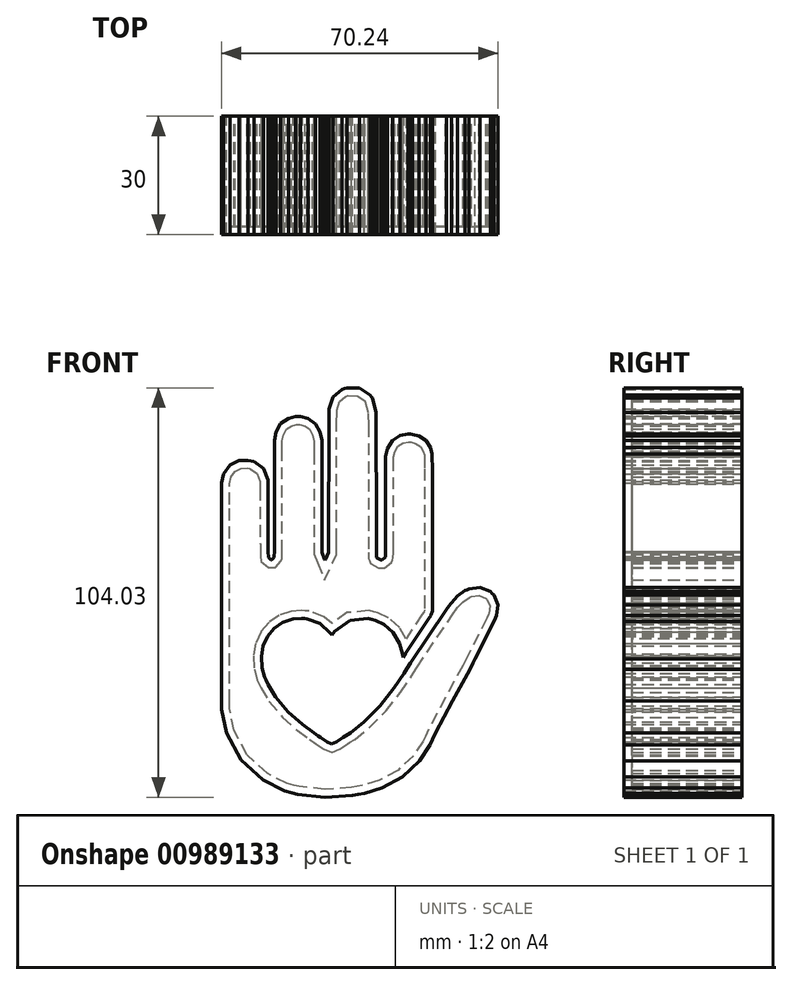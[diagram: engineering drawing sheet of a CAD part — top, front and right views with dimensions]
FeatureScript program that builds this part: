
annotation { "Feature Type Name" : "Feature", "Feature Type Description" : "" }
export const myFeature = defineFeature(function(context is Context, id is Id, definition is map)
    precondition{}
    {
        {
            var Q0;
            Q0=qCreatedBy(makeId("Front.planeOp"),FACE);
            var sketch = newSketch(context, id + "F0", { "sketchPlane" : qUnion([Q0])});
            skLineSegment(sketch, "E0", {"start": v(0.03, 0.14) * mm, "end": v(0.02, 0.14) * mm});
            skLineSegment(sketch, "E1", {"start": v(0.02, 0.14) * mm, "end": v(-0.03, 0.14) * mm});
            skLineSegment(sketch, "E2", {"start": v(-0.03, 0.14) * mm, "end": v(-0.07, 0.1) * mm});
            skLineSegment(sketch, "E3", {"start": v(-0.07, 0.1) * mm, "end": v(-0.07, 0.1) * mm});
            skLineSegment(sketch, "E4", {"start": v(-0.07, 0.1) * mm, "end": v(-0.08, 0.1) * mm});
            skLineSegment(sketch, "E5", {"start": v(-0.08, 0.1) * mm, "end": v(-0.1, 0.13) * mm});
            skLineSegment(sketch, "E6", {"start": v(-0.1, 0.13) * mm, "end": v(-0.14, 0.14) * mm});
            skLineSegment(sketch, "E7", {"start": v(-0.14, 0.14) * mm, "end": v(-0.14, 0.14) * mm});
            skLineSegment(sketch, "E8", {"start": v(-0.14, 0.14) * mm, "end": v(-0.15, 0.14) * mm});
            skLineSegment(sketch, "E9", {"start": v(-0.15, 0.14) * mm, "end": v(-0.17, 0.14) * mm});
            skLineSegment(sketch, "E10", {"start": v(-0.17, 0.14) * mm, "end": v(-0.2, 0.13) * mm});
            skLineSegment(sketch, "E11", {"start": v(-0.2, 0.13) * mm, "end": v(-0.22, 0.12) * mm});
            skLineSegment(sketch, "E12", {"start": v(-0.22, 0.12) * mm, "end": v(-0.24, 0.1) * mm});
            skLineSegment(sketch, "E13", {"start": v(-0.24, 0.1) * mm, "end": v(-0.25, 0.07) * mm});
            skLineSegment(sketch, "E14", {"start": v(-0.25, 0.07) * mm, "end": v(-0.25, 0.05) * mm});
            skLineSegment(sketch, "E15", {"start": v(-0.25, 0.05) * mm, "end": v(-0.25, 0.02) * mm});
            skLineSegment(sketch, "E16", {"start": v(-0.25, 0.02) * mm, "end": v(-0.24, 0) * mm});
            skLineSegment(sketch, "E17", {"start": v(-0.24, 0) * mm, "end": v(-0.24, -0.01) * mm});
            skLineSegment(sketch, "E18", {"start": v(-0.24, -0.01) * mm, "end": v(-0.24, -0.03) * mm});
            skLineSegment(sketch, "E19", {"start": v(-0.24, -0.03) * mm, "end": v(-0.22, -0.06) * mm});
            skLineSegment(sketch, "E20", {"start": v(-0.22, -0.06) * mm, "end": v(-0.18, -0.1) * mm});
            skLineSegment(sketch, "E21", {"start": v(-0.18, -0.1) * mm, "end": v(-0.15, -0.13) * mm});
            skLineSegment(sketch, "E22", {"start": v(-0.15, -0.13) * mm, "end": v(-0.12, -0.15) * mm});
            skLineSegment(sketch, "E23", {"start": v(-0.12, -0.15) * mm, "end": v(-0.1, -0.16) * mm});
            skLineSegment(sketch, "E24", {"start": v(-0.1, -0.16) * mm, "end": v(-0.1, -0.16) * mm});
            skLineSegment(sketch, "E25", {"start": v(-0.1, -0.16) * mm, "end": v(-0.09, -0.17) * mm});
            skLineSegment(sketch, "E26", {"start": v(-0.09, -0.17) * mm, "end": v(-0.07, -0.18) * mm});
            skLineSegment(sketch, "E27", {"start": v(-0.07, -0.18) * mm, "end": v(-0.06, -0.17) * mm});
            skLineSegment(sketch, "E28", {"start": v(-0.06, -0.17) * mm, "end": v(-0.04, -0.16) * mm});
            skLineSegment(sketch, "E29", {"start": v(-0.04, -0.16) * mm, "end": v(-0.04, -0.16) * mm});
            skLineSegment(sketch, "E30", {"start": v(-0.04, -0.16) * mm, "end": v(-0.03, -0.15) * mm});
            skLineSegment(sketch, "E31", {"start": v(-0.03, -0.15) * mm, "end": v(0, -0.12) * mm});
            skLineSegment(sketch, "E32", {"start": v(0, -0.12) * mm, "end": v(0.05, -0.08) * mm});
            skLineSegment(sketch, "E33", {"start": v(0.05, -0.08) * mm, "end": v(0.08, -0.03) * mm});
            skLineSegment(sketch, "E34", {"start": v(0.08, -0.03) * mm, "end": v(0.1, 0) * mm});
            skLineSegment(sketch, "E35", {"start": v(0.1, 0) * mm, "end": v(0.12, 0.01) * mm});
            skLineSegment(sketch, "E36", {"start": v(0.12, 0.01) * mm, "end": v(0.13, 0.03) * mm});
            skLineSegment(sketch, "E37", {"start": v(0.13, 0.03) * mm, "end": v(0.22, 0.17) * mm});
            skLineSegment(sketch, "E38", {"start": v(0.22, 0.17) * mm, "end": v(0.23, 0.18) * mm});
            skLineSegment(sketch, "E39", {"start": v(0.23, 0.18) * mm, "end": v(0.23, 0.18) * mm});
            skLineSegment(sketch, "E40", {"start": v(0.23, 0.18) * mm, "end": v(0.25, 0.2) * mm});
            skLineSegment(sketch, "E41", {"start": v(0.25, 0.2) * mm, "end": v(0.27, 0.21) * mm});
            skLineSegment(sketch, "E42", {"start": v(0.27, 0.21) * mm, "end": v(0.27, 0.21) * mm});
            skLineSegment(sketch, "E43", {"start": v(0.27, 0.21) * mm, "end": v(0.28, 0.22) * mm});
            skLineSegment(sketch, "E44", {"start": v(0.28, 0.22) * mm, "end": v(0.3, 0.22) * mm});
            skLineSegment(sketch, "E45", {"start": v(0.3, 0.22) * mm, "end": v(0.33, 0.21) * mm});
            skLineSegment(sketch, "E46", {"start": v(0.33, 0.21) * mm, "end": v(0.33, 0.2) * mm});
            skLineSegment(sketch, "E47", {"start": v(0.33, 0.2) * mm, "end": v(0.34, 0.2) * mm});
            skLineSegment(sketch, "E48", {"start": v(0.34, 0.2) * mm, "end": v(0.35, 0.18) * mm});
            skLineSegment(sketch, "E49", {"start": v(0.35, 0.18) * mm, "end": v(0.35, 0.15) * mm});
            skLineSegment(sketch, "E50", {"start": v(0.35, 0.15) * mm, "end": v(0.34, 0.14) * mm});
            skLineSegment(sketch, "E51", {"start": v(0.34, 0.14) * mm, "end": v(0.34, 0.13) * mm});
            skLineSegment(sketch, "E52", {"start": v(0.34, 0.13) * mm, "end": v(0.3, 0.04) * mm});
            skLineSegment(sketch, "E53", {"start": v(0.3, 0.04) * mm, "end": v(0.29, 0.03) * mm});
            skLineSegment(sketch, "E54", {"start": v(0.29, 0.03) * mm, "end": v(0.28, 0.01) * mm});
            skLineSegment(sketch, "E55", {"start": v(0.28, 0.01) * mm, "end": v(0.23, -0.07) * mm});
            skLineSegment(sketch, "E56", {"start": v(0.23, -0.07) * mm, "end": v(0.2, -0.15) * mm});
            skLineSegment(sketch, "E57", {"start": v(0.2, -0.15) * mm, "end": v(0.18, -0.17) * mm});
            skLineSegment(sketch, "E58", {"start": v(0.18, -0.17) * mm, "end": v(0.18, -0.18) * mm});
            skLineSegment(sketch, "E59", {"start": v(0.18, -0.18) * mm, "end": v(0.15, -0.22) * mm});
            skLineSegment(sketch, "E60", {"start": v(0.15, -0.22) * mm, "end": v(0.1, -0.26) * mm});
            skLineSegment(sketch, "E61", {"start": v(0.1, -0.26) * mm, "end": v(0.05, -0.29) * mm});
            skLineSegment(sketch, "E62", {"start": v(0.05, -0.29) * mm, "end": v(0, -0.3) * mm});
            skLineSegment(sketch, "E63", {"start": v(0, -0.3) * mm, "end": v(0, -0.3) * mm});
            skLineSegment(sketch, "E64", {"start": v(0, -0.3) * mm, "end": v(-0.02, -0.3) * mm});
            skLineSegment(sketch, "E65", {"start": v(-0.02, -0.3) * mm, "end": v(-0.1, -0.31) * mm});
            skLineSegment(sketch, "E66", {"start": v(-0.1, -0.31) * mm, "end": v(-0.16, -0.3) * mm});
            skLineSegment(sketch, "E67", {"start": v(-0.16, -0.3) * mm, "end": v(-0.17, -0.3) * mm});
            skLineSegment(sketch, "E68", {"start": v(-0.17, -0.3) * mm, "end": v(-0.2, -0.3) * mm});
            skLineSegment(sketch, "E69", {"start": v(-0.2, -0.3) * mm, "end": v(-0.25, -0.27) * mm});
            skLineSegment(sketch, "E70", {"start": v(-0.25, -0.27) * mm, "end": v(-0.3, -0.22) * mm});
            skLineSegment(sketch, "E71", {"start": v(-0.3, -0.22) * mm, "end": v(-0.34, -0.15) * mm});
            skLineSegment(sketch, "E72", {"start": v(-0.34, -0.15) * mm, "end": v(-0.35, -0.09) * mm});
            skLineSegment(sketch, "E73", {"start": v(-0.35, -0.09) * mm, "end": v(-0.35, -0.07) * mm});
            skLineSegment(sketch, "E74", {"start": v(-0.35, -0.07) * mm, "end": v(-0.35, -0.02) * mm});
            skLineSegment(sketch, "E75", {"start": v(-0.35, -0.02) * mm, "end": v(-0.35, 0.43) * mm});
            skLineSegment(sketch, "E76", {"start": v(-0.35, 0.43) * mm, "end": v(-0.35, 0.48) * mm});
            skLineSegment(sketch, "E77", {"start": v(-0.35, 0.48) * mm, "end": v(-0.35, 0.49) * mm});
            skLineSegment(sketch, "E78", {"start": v(-0.35, 0.49) * mm, "end": v(-0.35, 0.5) * mm});
            skLineSegment(sketch, "E79", {"start": v(-0.35, 0.5) * mm, "end": v(-0.33, 0.53) * mm});
            skLineSegment(sketch, "E80", {"start": v(-0.33, 0.53) * mm, "end": v(-0.3, 0.54) * mm});
            skLineSegment(sketch, "E81", {"start": v(-0.3, 0.54) * mm, "end": v(-0.29, 0.54) * mm});
            skLineSegment(sketch, "E82", {"start": v(-0.29, 0.54) * mm, "end": v(-0.28, 0.54) * mm});
            skLineSegment(sketch, "E83", {"start": v(-0.28, 0.54) * mm, "end": v(-0.27, 0.54) * mm});
            skLineSegment(sketch, "E84", {"start": v(-0.27, 0.54) * mm, "end": v(-0.25, 0.52) * mm});
            skLineSegment(sketch, "E85", {"start": v(-0.25, 0.52) * mm, "end": v(-0.24, 0.5) * mm});
            skLineSegment(sketch, "E86", {"start": v(-0.24, 0.5) * mm, "end": v(-0.24, 0.49) * mm});
            skLineSegment(sketch, "E87", {"start": v(-0.24, 0.49) * mm, "end": v(-0.24, 0.47) * mm});
            skLineSegment(sketch, "E88", {"start": v(-0.24, 0.47) * mm, "end": v(-0.24, 0.33) * mm});
            skLineSegment(sketch, "E89", {"start": v(-0.24, 0.33) * mm, "end": v(-0.23, 0.32) * mm});
            skLineSegment(sketch, "E90", {"start": v(-0.23, 0.32) * mm, "end": v(-0.23, 0.31) * mm});
            skLineSegment(sketch, "E91", {"start": v(-0.23, 0.31) * mm, "end": v(-0.23, 0.3) * mm});
            skLineSegment(sketch, "E92", {"start": v(-0.23, 0.3) * mm, "end": v(-0.23, 0.3) * mm});
            skLineSegment(sketch, "E93", {"start": v(-0.23, 0.3) * mm, "end": v(-0.22, 0.3) * mm});
            skLineSegment(sketch, "E94", {"start": v(-0.22, 0.3) * mm, "end": v(-0.22, 0.3) * mm});
            skLineSegment(sketch, "E95", {"start": v(-0.22, 0.3) * mm, "end": v(-0.22, 0.31) * mm});
            skLineSegment(sketch, "E96", {"start": v(-0.22, 0.31) * mm, "end": v(-0.22, 0.32) * mm});
            skLineSegment(sketch, "E97", {"start": v(-0.22, 0.32) * mm, "end": v(-0.22, 0.38) * mm});
            skLineSegment(sketch, "E98", {"start": v(-0.22, 0.38) * mm, "end": v(-0.22, 0.56) * mm});
            skLineSegment(sketch, "E99", {"start": v(-0.22, 0.56) * mm, "end": v(-0.22, 0.59) * mm});
            skLineSegment(sketch, "E100", {"start": v(-0.22, 0.59) * mm, "end": v(-0.22, 0.6) * mm});
            skLineSegment(sketch, "E101", {"start": v(-0.22, 0.6) * mm, "end": v(-0.22, 0.62) * mm});
            skLineSegment(sketch, "E102", {"start": v(-0.22, 0.62) * mm, "end": v(-0.2, 0.64) * mm});
            skLineSegment(sketch, "E103", {"start": v(-0.2, 0.64) * mm, "end": v(-0.18, 0.65) * mm});
            skLineSegment(sketch, "E104", {"start": v(-0.18, 0.65) * mm, "end": v(-0.16, 0.65) * mm});
            skLineSegment(sketch, "E105", {"start": v(-0.16, 0.65) * mm, "end": v(-0.16, 0.65) * mm});
            skLineSegment(sketch, "E106", {"start": v(-0.16, 0.65) * mm, "end": v(-0.15, 0.65) * mm});
            skLineSegment(sketch, "E107", {"start": v(-0.15, 0.65) * mm, "end": v(-0.13, 0.65) * mm});
            skLineSegment(sketch, "E108", {"start": v(-0.13, 0.65) * mm, "end": v(-0.11, 0.64) * mm});
            skLineSegment(sketch, "E109", {"start": v(-0.11, 0.64) * mm, "end": v(-0.1, 0.62) * mm});
            skLineSegment(sketch, "E110", {"start": v(-0.1, 0.62) * mm, "end": v(-0.1, 0.6) * mm});
            skLineSegment(sketch, "E111", {"start": v(-0.1, 0.6) * mm, "end": v(-0.1, 0.59) * mm});
            skLineSegment(sketch, "E112", {"start": v(-0.1, 0.59) * mm, "end": v(-0.1, 0.56) * mm});
            skLineSegment(sketch, "E113", {"start": v(-0.1, 0.56) * mm, "end": v(-0.1, 0.33) * mm});
            skLineSegment(sketch, "E114", {"start": v(-0.1, 0.33) * mm, "end": v(-0.1, 0.31) * mm});
            skLineSegment(sketch, "E115", {"start": v(-0.1, 0.31) * mm, "end": v(-0.1, 0.3) * mm});
            skLineSegment(sketch, "E116", {"start": v(-0.1, 0.3) * mm, "end": v(-0.1, 0.3) * mm});
            skLineSegment(sketch, "E117", {"start": v(-0.1, 0.3) * mm, "end": v(-0.09, 0.3) * mm});
            skLineSegment(sketch, "E118", {"start": v(-0.09, 0.3) * mm, "end": v(-0.08, 0.3) * mm});
            skLineSegment(sketch, "E119", {"start": v(-0.08, 0.3) * mm, "end": v(-0.08, 0.31) * mm});
            skLineSegment(sketch, "E120", {"start": v(-0.08, 0.31) * mm, "end": v(-0.08, 0.34) * mm});
            skLineSegment(sketch, "E121", {"start": v(-0.08, 0.34) * mm, "end": v(-0.08, 0.64) * mm});
            skLineSegment(sketch, "E122", {"start": v(-0.08, 0.64) * mm, "end": v(-0.08, 0.67) * mm});
            skLineSegment(sketch, "E123", {"start": v(-0.08, 0.67) * mm, "end": v(-0.08, 0.67) * mm});
            skLineSegment(sketch, "E124", {"start": v(-0.08, 0.67) * mm, "end": v(-0.07, 0.7) * mm});
            skLineSegment(sketch, "E125", {"start": v(-0.07, 0.7) * mm, "end": v(-0.05, 0.72) * mm});
            skLineSegment(sketch, "E126", {"start": v(-0.05, 0.72) * mm, "end": v(-0.04, 0.73) * mm});
            skLineSegment(sketch, "E127", {"start": v(-0.04, 0.73) * mm, "end": v(-0.04, 0.73) * mm});
            skLineSegment(sketch, "E128", {"start": v(-0.04, 0.73) * mm, "end": v(0, 0.73) * mm});
            skLineSegment(sketch, "E129", {"start": v(0, 0.73) * mm, "end": v(0.02, 0.71) * mm});
            skLineSegment(sketch, "E130", {"start": v(0.02, 0.71) * mm, "end": v(0.03, 0.7) * mm});
            skLineSegment(sketch, "E131", {"start": v(0.03, 0.7) * mm, "end": v(0.03, 0.7) * mm});
            skLineSegment(sketch, "E132", {"start": v(0.03, 0.7) * mm, "end": v(0.04, 0.67) * mm});
            skLineSegment(sketch, "E133", {"start": v(0.04, 0.67) * mm, "end": v(0.04, 0.66) * mm});
            skLineSegment(sketch, "E134", {"start": v(0.04, 0.66) * mm, "end": v(0.04, 0.63) * mm});
            skLineSegment(sketch, "E135", {"start": v(0.04, 0.63) * mm, "end": v(0.04, 0.4) * mm});
            skLineSegment(sketch, "E136", {"start": v(0.04, 0.4) * mm, "end": v(0.04, 0.32) * mm});
            skLineSegment(sketch, "E137", {"start": v(0.04, 0.32) * mm, "end": v(0.04, 0.31) * mm});
            skLineSegment(sketch, "E138", {"start": v(0.04, 0.31) * mm, "end": v(0.04, 0.3) * mm});
            skLineSegment(sketch, "E139", {"start": v(0.04, 0.3) * mm, "end": v(0.04, 0.3) * mm});
            skLineSegment(sketch, "E140", {"start": v(0.04, 0.3) * mm, "end": v(0.05, 0.3) * mm});
            skLineSegment(sketch, "E141", {"start": v(0.05, 0.3) * mm, "end": v(0.05, 0.3) * mm});
            skLineSegment(sketch, "E142", {"start": v(0.05, 0.3) * mm, "end": v(0.06, 0.3) * mm});
            skLineSegment(sketch, "E143", {"start": v(0.06, 0.3) * mm, "end": v(0.06, 0.3) * mm});
            skLineSegment(sketch, "E144", {"start": v(0.06, 0.3) * mm, "end": v(0.06, 0.31) * mm});
            skLineSegment(sketch, "E145", {"start": v(0.06, 0.31) * mm, "end": v(0.06, 0.33) * mm});
            skLineSegment(sketch, "E146", {"start": v(0.06, 0.33) * mm, "end": v(0.06, 0.53) * mm});
            skLineSegment(sketch, "E147", {"start": v(0.06, 0.53) * mm, "end": v(0.06, 0.55) * mm});
            skLineSegment(sketch, "E148", {"start": v(0.06, 0.55) * mm, "end": v(0.06, 0.55) * mm});
            skLineSegment(sketch, "E149", {"start": v(0.06, 0.55) * mm, "end": v(0.07, 0.57) * mm});
            skLineSegment(sketch, "E150", {"start": v(0.07, 0.57) * mm, "end": v(0.08, 0.6) * mm});
            skLineSegment(sketch, "E151", {"start": v(0.08, 0.6) * mm, "end": v(0.1, 0.6) * mm});
            skLineSegment(sketch, "E152", {"start": v(0.1, 0.6) * mm, "end": v(0.12, 0.61) * mm});
            skLineSegment(sketch, "E153", {"start": v(0.12, 0.61) * mm, "end": v(0.13, 0.61) * mm});
            skLineSegment(sketch, "E154", {"start": v(0.13, 0.61) * mm, "end": v(0.13, 0.6) * mm});
            skLineSegment(sketch, "E155", {"start": v(0.13, 0.6) * mm, "end": v(0.15, 0.6) * mm});
            skLineSegment(sketch, "E156", {"start": v(0.15, 0.6) * mm, "end": v(0.17, 0.6) * mm});
            skLineSegment(sketch, "E157", {"start": v(0.17, 0.6) * mm, "end": v(0.18, 0.58) * mm});
            skLineSegment(sketch, "E158", {"start": v(0.18, 0.58) * mm, "end": v(0.18, 0.56) * mm});
            skLineSegment(sketch, "E159", {"start": v(0.18, 0.56) * mm, "end": v(0.18, 0.55) * mm});
            skLineSegment(sketch, "E160", {"start": v(0.18, 0.55) * mm, "end": v(0.18, 0.52) * mm});
            skLineSegment(sketch, "E161", {"start": v(0.18, 0.52) * mm, "end": v(0.18, 0.2) * mm});
            skLineSegment(sketch, "E162", {"start": v(0.18, 0.2) * mm, "end": v(0.18, 0.16) * mm});
            skLineSegment(sketch, "E163", {"start": v(0.18, 0.16) * mm, "end": v(0.18, 0.16) * mm});
            skLineSegment(sketch, "E164", {"start": v(0.18, 0.16) * mm, "end": v(0.18, 0.15) * mm});
            skLineSegment(sketch, "E165", {"start": v(0.18, 0.15) * mm, "end": v(0.18, 0.15) * mm});
            skLineSegment(sketch, "E166", {"start": v(0.18, 0.15) * mm, "end": v(0.17, 0.14) * mm});
            skLineSegment(sketch, "E167", {"start": v(0.17, 0.14) * mm, "end": v(0.11, 0.05) * mm});
            skLineSegment(sketch, "E168", {"start": v(0.11, 0.05) * mm, "end": v(0.1, 0.04) * mm});
            skLineSegment(sketch, "E169", {"start": v(0.1, 0.04) * mm, "end": v(0.1, 0.05) * mm});
            skLineSegment(sketch, "E170", {"start": v(0.1, 0.05) * mm, "end": v(0.1, 0.08) * mm});
            skLineSegment(sketch, "E171", {"start": v(0.1, 0.08) * mm, "end": v(0.08, 0.1) * mm});
            skLineSegment(sketch, "E172", {"start": v(0.08, 0.1) * mm, "end": v(0.06, 0.13) * mm});
            skLineSegment(sketch, "E173", {"start": v(0.06, 0.13) * mm, "end": v(0.04, 0.14) * mm});
            skLineSegment(sketch, "E174", {"start": v(0.04, 0.14) * mm, "end": v(0.03, 0.14) * mm});
            skSolve(sketch);
        }
        {
            var Q0;
            Q0=makeQuery(id+"F0.imprint","IMPRINT",FACE,{"disambiguationData":[TD([[makeQuery(id+"F0.imprint","IMPRINT",EDGE,{"derivedFrom":sQuery(id+"F0.wireOp",EDGE,"E0")}),-1.0]])]});
            extrude(context, id + "F1", {"entities" : qUnion([Q0]), "depth" : 0.2 * mm, "offsetDistance" : 25 * mm});
        }
        {
            var Q0;
            Q0=makeQuery(id+"F1.opExtrude","SWEPT_BODY",BODY,{"disambiguationData":[OSD([sQuery(id+"F0.wireOp",EDGE,"E0"),sQuery(id+"F0.wireOp",EDGE,"E1"),sQuery(id+"F0.wireOp",EDGE,"E2"),sQuery(id+"F0.wireOp",EDGE,"E3"),sQuery(id+"F0.wireOp",EDGE,"E4"),sQuery(id+"F0.wireOp",EDGE,"E5"),sQuery(id+"F0.wireOp",EDGE,"E6"),sQuery(id+"F0.wireOp",EDGE,"E7"),sQuery(id+"F0.wireOp",EDGE,"E8"),sQuery(id+"F0.wireOp",EDGE,"E9"),sQuery(id+"F0.wireOp",EDGE,"E10"),sQuery(id+"F0.wireOp",EDGE,"E11"),sQuery(id+"F0.wireOp",EDGE,"E12"),sQuery(id+"F0.wireOp",EDGE,"E13"),sQuery(id+"F0.wireOp",EDGE,"E14"),sQuery(id+"F0.wireOp",EDGE,"E15"),sQuery(id+"F0.wireOp",EDGE,"E16"),sQuery(id+"F0.wireOp",EDGE,"E17"),sQuery(id+"F0.wireOp",EDGE,"E18"),sQuery(id+"F0.wireOp",EDGE,"E19"),sQuery(id+"F0.wireOp",EDGE,"E20"),sQuery(id+"F0.wireOp",EDGE,"E21"),sQuery(id+"F0.wireOp",EDGE,"E22"),sQuery(id+"F0.wireOp",EDGE,"E23"),sQuery(id+"F0.wireOp",EDGE,"E24"),sQuery(id+"F0.wireOp",EDGE,"E25"),sQuery(id+"F0.wireOp",EDGE,"E26"),sQuery(id+"F0.wireOp",EDGE,"E27"),sQuery(id+"F0.wireOp",EDGE,"E28"),sQuery(id+"F0.wireOp",EDGE,"E29"),sQuery(id+"F0.wireOp",EDGE,"E30"),sQuery(id+"F0.wireOp",EDGE,"E31"),sQuery(id+"F0.wireOp",EDGE,"E32"),sQuery(id+"F0.wireOp",EDGE,"E33"),sQuery(id+"F0.wireOp",EDGE,"E34"),sQuery(id+"F0.wireOp",EDGE,"E35"),sQuery(id+"F0.wireOp",EDGE,"E36"),sQuery(id+"F0.wireOp",EDGE,"E37"),sQuery(id+"F0.wireOp",EDGE,"E38"),sQuery(id+"F0.wireOp",EDGE,"E39"),sQuery(id+"F0.wireOp",EDGE,"E40"),sQuery(id+"F0.wireOp",EDGE,"E41"),sQuery(id+"F0.wireOp",EDGE,"E42"),sQuery(id+"F0.wireOp",EDGE,"E43"),sQuery(id+"F0.wireOp",EDGE,"E44"),sQuery(id+"F0.wireOp",EDGE,"E45"),sQuery(id+"F0.wireOp",EDGE,"E46"),sQuery(id+"F0.wireOp",EDGE,"E47"),sQuery(id+"F0.wireOp",EDGE,"E48"),sQuery(id+"F0.wireOp",EDGE,"E49"),sQuery(id+"F0.wireOp",EDGE,"E50"),sQuery(id+"F0.wireOp",EDGE,"E51"),sQuery(id+"F0.wireOp",EDGE,"E52"),sQuery(id+"F0.wireOp",EDGE,"E53"),sQuery(id+"F0.wireOp",EDGE,"E54"),sQuery(id+"F0.wireOp",EDGE,"E55"),sQuery(id+"F0.wireOp",EDGE,"E56"),sQuery(id+"F0.wireOp",EDGE,"E57"),sQuery(id+"F0.wireOp",EDGE,"E58"),sQuery(id+"F0.wireOp",EDGE,"E59"),sQuery(id+"F0.wireOp",EDGE,"E60"),sQuery(id+"F0.wireOp",EDGE,"E61"),sQuery(id+"F0.wireOp",EDGE,"E62"),sQuery(id+"F0.wireOp",EDGE,"E63"),sQuery(id+"F0.wireOp",EDGE,"E64"),sQuery(id+"F0.wireOp",EDGE,"E65"),sQuery(id+"F0.wireOp",EDGE,"E66"),sQuery(id+"F0.wireOp",EDGE,"E67"),sQuery(id+"F0.wireOp",EDGE,"E68"),sQuery(id+"F0.wireOp",EDGE,"E69"),sQuery(id+"F0.wireOp",EDGE,"E70"),sQuery(id+"F0.wireOp",EDGE,"E71"),sQuery(id+"F0.wireOp",EDGE,"E72"),sQuery(id+"F0.wireOp",EDGE,"E73"),sQuery(id+"F0.wireOp",EDGE,"E74"),sQuery(id+"F0.wireOp",EDGE,"E75"),sQuery(id+"F0.wireOp",EDGE,"E76"),sQuery(id+"F0.wireOp",EDGE,"E77"),sQuery(id+"F0.wireOp",EDGE,"E78"),sQuery(id+"F0.wireOp",EDGE,"E79"),sQuery(id+"F0.wireOp",EDGE,"E80"),sQuery(id+"F0.wireOp",EDGE,"E81"),sQuery(id+"F0.wireOp",EDGE,"E82"),sQuery(id+"F0.wireOp",EDGE,"E83"),sQuery(id+"F0.wireOp",EDGE,"E84"),sQuery(id+"F0.wireOp",EDGE,"E85"),sQuery(id+"F0.wireOp",EDGE,"E86"),sQuery(id+"F0.wireOp",EDGE,"E87"),sQuery(id+"F0.wireOp",EDGE,"E88"),sQuery(id+"F0.wireOp",EDGE,"E89"),sQuery(id+"F0.wireOp",EDGE,"E90"),sQuery(id+"F0.wireOp",EDGE,"E91"),sQuery(id+"F0.wireOp",EDGE,"E92"),sQuery(id+"F0.wireOp",EDGE,"E92"),sQuery(id+"F0.wireOp",EDGE,"E92"),sQuery(id+"F0.wireOp",EDGE,"E92"),sQuery(id+"F0.wireOp",EDGE,"E92"),sQuery(id+"F0.wireOp",EDGE,"E93"),sQuery(id+"F0.wireOp",EDGE,"E94"),sQuery(id+"F0.wireOp",EDGE,"E94"),sQuery(id+"F0.wireOp",EDGE,"E95"),sQuery(id+"F0.wireOp",EDGE,"E96"),sQuery(id+"F0.wireOp",EDGE,"E97"),sQuery(id+"F0.wireOp",EDGE,"E98"),sQuery(id+"F0.wireOp",EDGE,"E99"),sQuery(id+"F0.wireOp",EDGE,"E100"),sQuery(id+"F0.wireOp",EDGE,"E101"),sQuery(id+"F0.wireOp",EDGE,"E102"),sQuery(id+"F0.wireOp",EDGE,"E103"),sQuery(id+"F0.wireOp",EDGE,"E104"),sQuery(id+"F0.wireOp",EDGE,"E105"),sQuery(id+"F0.wireOp",EDGE,"E106"),sQuery(id+"F0.wireOp",EDGE,"E107"),sQuery(id+"F0.wireOp",EDGE,"E108"),sQuery(id+"F0.wireOp",EDGE,"E109"),sQuery(id+"F0.wireOp",EDGE,"E110"),sQuery(id+"F0.wireOp",EDGE,"E111"),sQuery(id+"F0.wireOp",EDGE,"E112"),sQuery(id+"F0.wireOp",EDGE,"E113"),sQuery(id+"F0.wireOp",EDGE,"E114"),sQuery(id+"F0.wireOp",EDGE,"E115"),sQuery(id+"F0.wireOp",EDGE,"E116"),sQuery(id+"F0.wireOp",EDGE,"E116"),sQuery(id+"F0.wireOp",EDGE,"E117"),sQuery(id+"F0.wireOp",EDGE,"E118"),sQuery(id+"F0.wireOp",EDGE,"E119"),sQuery(id+"F0.wireOp",EDGE,"E120"),sQuery(id+"F0.wireOp",EDGE,"E121"),sQuery(id+"F0.wireOp",EDGE,"E122"),sQuery(id+"F0.wireOp",EDGE,"E123"),sQuery(id+"F0.wireOp",EDGE,"E124"),sQuery(id+"F0.wireOp",EDGE,"E125"),sQuery(id+"F0.wireOp",EDGE,"E126"),sQuery(id+"F0.wireOp",EDGE,"E127"),sQuery(id+"F0.wireOp",EDGE,"E128"),sQuery(id+"F0.wireOp",EDGE,"E129"),sQuery(id+"F0.wireOp",EDGE,"E130"),sQuery(id+"F0.wireOp",EDGE,"E131"),sQuery(id+"F0.wireOp",EDGE,"E132"),sQuery(id+"F0.wireOp",EDGE,"E133"),sQuery(id+"F0.wireOp",EDGE,"E134"),sQuery(id+"F0.wireOp",EDGE,"E135"),sQuery(id+"F0.wireOp",EDGE,"E136"),sQuery(id+"F0.wireOp",EDGE,"E137"),sQuery(id+"F0.wireOp",EDGE,"E138"),sQuery(id+"F0.wireOp",EDGE,"E139"),sQuery(id+"F0.wireOp",EDGE,"E139"),sQuery(id+"F0.wireOp",EDGE,"E140"),sQuery(id+"F0.wireOp",EDGE,"E141"),sQuery(id+"F0.wireOp",EDGE,"E141"),sQuery(id+"F0.wireOp",EDGE,"E142"),sQuery(id+"F0.wireOp",EDGE,"E143"),sQuery(id+"F0.wireOp",EDGE,"E143"),sQuery(id+"F0.wireOp",EDGE,"E143"),sQuery(id+"F0.wireOp",EDGE,"E144"),sQuery(id+"F0.wireOp",EDGE,"E145"),sQuery(id+"F0.wireOp",EDGE,"E146"),sQuery(id+"F0.wireOp",EDGE,"E147"),sQuery(id+"F0.wireOp",EDGE,"E148"),sQuery(id+"F0.wireOp",EDGE,"E149"),sQuery(id+"F0.wireOp",EDGE,"E150"),sQuery(id+"F0.wireOp",EDGE,"E151"),sQuery(id+"F0.wireOp",EDGE,"E152"),sQuery(id+"F0.wireOp",EDGE,"E153"),sQuery(id+"F0.wireOp",EDGE,"E154"),sQuery(id+"F0.wireOp",EDGE,"E155"),sQuery(id+"F0.wireOp",EDGE,"E156"),sQuery(id+"F0.wireOp",EDGE,"E157"),sQuery(id+"F0.wireOp",EDGE,"E158"),sQuery(id+"F0.wireOp",EDGE,"E159"),sQuery(id+"F0.wireOp",EDGE,"E160"),sQuery(id+"F0.wireOp",EDGE,"E161"),sQuery(id+"F0.wireOp",EDGE,"E162"),sQuery(id+"F0.wireOp",EDGE,"E163"),sQuery(id+"F0.wireOp",EDGE,"E164"),sQuery(id+"F0.wireOp",EDGE,"E165"),sQuery(id+"F0.wireOp",EDGE,"E166"),sQuery(id+"F0.wireOp",EDGE,"E167"),sQuery(id+"F0.wireOp",EDGE,"E168"),sQuery(id+"F0.wireOp",EDGE,"E169"),sQuery(id+"F0.wireOp",EDGE,"E170"),sQuery(id+"F0.wireOp",EDGE,"E171"),sQuery(id+"F0.wireOp",EDGE,"E172"),sQuery(id+"F0.wireOp",EDGE,"E173"),sQuery(id+"F0.wireOp",EDGE,"E174")])]});
            var Q1;
            Q1=qCreatedBy(makeId("Origin.pointOp"),VERTEX);
            transform(context, id + "F2", {"entities" : qUnion([Q0]), "transformType" : TransformType.SCALE_UNIFORMLY, "scale" : 100, "scalePoint" : qUnion([Q1]), "makeCopy" : false});
        }
        {
            var Q0;
            Q0=makeQuery(id+"F1.opExtrude","CAP_FACE",FACE,{"disambiguationData":[OSD([sQuery(id+"F0.wireOp",EDGE,"E0"),sQuery(id+"F0.wireOp",EDGE,"E1"),sQuery(id+"F0.wireOp",EDGE,"E2"),sQuery(id+"F0.wireOp",EDGE,"E3"),sQuery(id+"F0.wireOp",EDGE,"E4"),sQuery(id+"F0.wireOp",EDGE,"E5"),sQuery(id+"F0.wireOp",EDGE,"E6"),sQuery(id+"F0.wireOp",EDGE,"E7"),sQuery(id+"F0.wireOp",EDGE,"E8"),sQuery(id+"F0.wireOp",EDGE,"E9"),sQuery(id+"F0.wireOp",EDGE,"E10"),sQuery(id+"F0.wireOp",EDGE,"E11"),sQuery(id+"F0.wireOp",EDGE,"E12"),sQuery(id+"F0.wireOp",EDGE,"E13"),sQuery(id+"F0.wireOp",EDGE,"E14"),sQuery(id+"F0.wireOp",EDGE,"E15"),sQuery(id+"F0.wireOp",EDGE,"E16"),sQuery(id+"F0.wireOp",EDGE,"E17"),sQuery(id+"F0.wireOp",EDGE,"E18"),sQuery(id+"F0.wireOp",EDGE,"E19"),sQuery(id+"F0.wireOp",EDGE,"E20"),sQuery(id+"F0.wireOp",EDGE,"E21"),sQuery(id+"F0.wireOp",EDGE,"E22"),sQuery(id+"F0.wireOp",EDGE,"E23"),sQuery(id+"F0.wireOp",EDGE,"E24"),sQuery(id+"F0.wireOp",EDGE,"E25"),sQuery(id+"F0.wireOp",EDGE,"E26"),sQuery(id+"F0.wireOp",EDGE,"E27"),sQuery(id+"F0.wireOp",EDGE,"E28"),sQuery(id+"F0.wireOp",EDGE,"E29"),sQuery(id+"F0.wireOp",EDGE,"E30"),sQuery(id+"F0.wireOp",EDGE,"E31"),sQuery(id+"F0.wireOp",EDGE,"E32"),sQuery(id+"F0.wireOp",EDGE,"E33"),sQuery(id+"F0.wireOp",EDGE,"E34"),sQuery(id+"F0.wireOp",EDGE,"E35"),sQuery(id+"F0.wireOp",EDGE,"E36"),sQuery(id+"F0.wireOp",EDGE,"E37"),sQuery(id+"F0.wireOp",EDGE,"E38"),sQuery(id+"F0.wireOp",EDGE,"E39"),sQuery(id+"F0.wireOp",EDGE,"E40"),sQuery(id+"F0.wireOp",EDGE,"E41"),sQuery(id+"F0.wireOp",EDGE,"E42"),sQuery(id+"F0.wireOp",EDGE,"E43"),sQuery(id+"F0.wireOp",EDGE,"E44"),sQuery(id+"F0.wireOp",EDGE,"E45"),sQuery(id+"F0.wireOp",EDGE,"E46"),sQuery(id+"F0.wireOp",EDGE,"E47"),sQuery(id+"F0.wireOp",EDGE,"E48"),sQuery(id+"F0.wireOp",EDGE,"E49"),sQuery(id+"F0.wireOp",EDGE,"E50"),sQuery(id+"F0.wireOp",EDGE,"E51"),sQuery(id+"F0.wireOp",EDGE,"E52"),sQuery(id+"F0.wireOp",EDGE,"E53"),sQuery(id+"F0.wireOp",EDGE,"E54"),sQuery(id+"F0.wireOp",EDGE,"E55"),sQuery(id+"F0.wireOp",EDGE,"E56"),sQuery(id+"F0.wireOp",EDGE,"E57"),sQuery(id+"F0.wireOp",EDGE,"E58"),sQuery(id+"F0.wireOp",EDGE,"E59"),sQuery(id+"F0.wireOp",EDGE,"E60"),sQuery(id+"F0.wireOp",EDGE,"E61"),sQuery(id+"F0.wireOp",EDGE,"E62"),sQuery(id+"F0.wireOp",EDGE,"E63"),sQuery(id+"F0.wireOp",EDGE,"E64"),sQuery(id+"F0.wireOp",EDGE,"E65"),sQuery(id+"F0.wireOp",EDGE,"E66"),sQuery(id+"F0.wireOp",EDGE,"E67"),sQuery(id+"F0.wireOp",EDGE,"E68"),sQuery(id+"F0.wireOp",EDGE,"E69"),sQuery(id+"F0.wireOp",EDGE,"E70"),sQuery(id+"F0.wireOp",EDGE,"E71"),sQuery(id+"F0.wireOp",EDGE,"E72"),sQuery(id+"F0.wireOp",EDGE,"E73"),sQuery(id+"F0.wireOp",EDGE,"E74"),sQuery(id+"F0.wireOp",EDGE,"E75"),sQuery(id+"F0.wireOp",EDGE,"E76"),sQuery(id+"F0.wireOp",EDGE,"E77"),sQuery(id+"F0.wireOp",EDGE,"E78"),sQuery(id+"F0.wireOp",EDGE,"E79"),sQuery(id+"F0.wireOp",EDGE,"E80"),sQuery(id+"F0.wireOp",EDGE,"E81"),sQuery(id+"F0.wireOp",EDGE,"E82"),sQuery(id+"F0.wireOp",EDGE,"E83"),sQuery(id+"F0.wireOp",EDGE,"E84"),sQuery(id+"F0.wireOp",EDGE,"E85"),sQuery(id+"F0.wireOp",EDGE,"E86"),sQuery(id+"F0.wireOp",EDGE,"E87"),sQuery(id+"F0.wireOp",EDGE,"E88"),sQuery(id+"F0.wireOp",EDGE,"E89"),sQuery(id+"F0.wireOp",EDGE,"E90"),sQuery(id+"F0.wireOp",EDGE,"E91"),sQuery(id+"F0.wireOp",EDGE,"E92"),sQuery(id+"F0.wireOp",EDGE,"E92"),sQuery(id+"F0.wireOp",EDGE,"E92"),sQuery(id+"F0.wireOp",EDGE,"E92"),sQuery(id+"F0.wireOp",EDGE,"E92"),sQuery(id+"F0.wireOp",EDGE,"E93"),sQuery(id+"F0.wireOp",EDGE,"E94"),sQuery(id+"F0.wireOp",EDGE,"E94"),sQuery(id+"F0.wireOp",EDGE,"E95"),sQuery(id+"F0.wireOp",EDGE,"E96"),sQuery(id+"F0.wireOp",EDGE,"E97"),sQuery(id+"F0.wireOp",EDGE,"E98"),sQuery(id+"F0.wireOp",EDGE,"E99"),sQuery(id+"F0.wireOp",EDGE,"E100"),sQuery(id+"F0.wireOp",EDGE,"E101"),sQuery(id+"F0.wireOp",EDGE,"E102"),sQuery(id+"F0.wireOp",EDGE,"E103"),sQuery(id+"F0.wireOp",EDGE,"E104"),sQuery(id+"F0.wireOp",EDGE,"E105"),sQuery(id+"F0.wireOp",EDGE,"E106"),sQuery(id+"F0.wireOp",EDGE,"E107"),sQuery(id+"F0.wireOp",EDGE,"E108"),sQuery(id+"F0.wireOp",EDGE,"E109"),sQuery(id+"F0.wireOp",EDGE,"E110"),sQuery(id+"F0.wireOp",EDGE,"E111"),sQuery(id+"F0.wireOp",EDGE,"E112"),sQuery(id+"F0.wireOp",EDGE,"E113"),sQuery(id+"F0.wireOp",EDGE,"E114"),sQuery(id+"F0.wireOp",EDGE,"E115"),sQuery(id+"F0.wireOp",EDGE,"E116"),sQuery(id+"F0.wireOp",EDGE,"E116"),sQuery(id+"F0.wireOp",EDGE,"E117"),sQuery(id+"F0.wireOp",EDGE,"E118"),sQuery(id+"F0.wireOp",EDGE,"E119"),sQuery(id+"F0.wireOp",EDGE,"E120"),sQuery(id+"F0.wireOp",EDGE,"E121"),sQuery(id+"F0.wireOp",EDGE,"E122"),sQuery(id+"F0.wireOp",EDGE,"E123"),sQuery(id+"F0.wireOp",EDGE,"E124"),sQuery(id+"F0.wireOp",EDGE,"E125"),sQuery(id+"F0.wireOp",EDGE,"E126"),sQuery(id+"F0.wireOp",EDGE,"E127"),sQuery(id+"F0.wireOp",EDGE,"E128"),sQuery(id+"F0.wireOp",EDGE,"E129"),sQuery(id+"F0.wireOp",EDGE,"E130"),sQuery(id+"F0.wireOp",EDGE,"E131"),sQuery(id+"F0.wireOp",EDGE,"E132"),sQuery(id+"F0.wireOp",EDGE,"E133"),sQuery(id+"F0.wireOp",EDGE,"E134"),sQuery(id+"F0.wireOp",EDGE,"E135"),sQuery(id+"F0.wireOp",EDGE,"E136"),sQuery(id+"F0.wireOp",EDGE,"E137"),sQuery(id+"F0.wireOp",EDGE,"E138"),sQuery(id+"F0.wireOp",EDGE,"E139"),sQuery(id+"F0.wireOp",EDGE,"E139"),sQuery(id+"F0.wireOp",EDGE,"E140"),sQuery(id+"F0.wireOp",EDGE,"E141"),sQuery(id+"F0.wireOp",EDGE,"E141"),sQuery(id+"F0.wireOp",EDGE,"E142"),sQuery(id+"F0.wireOp",EDGE,"E143"),sQuery(id+"F0.wireOp",EDGE,"E143"),sQuery(id+"F0.wireOp",EDGE,"E143"),sQuery(id+"F0.wireOp",EDGE,"E144"),sQuery(id+"F0.wireOp",EDGE,"E145"),sQuery(id+"F0.wireOp",EDGE,"E146"),sQuery(id+"F0.wireOp",EDGE,"E147"),sQuery(id+"F0.wireOp",EDGE,"E148"),sQuery(id+"F0.wireOp",EDGE,"E149"),sQuery(id+"F0.wireOp",EDGE,"E150"),sQuery(id+"F0.wireOp",EDGE,"E151"),sQuery(id+"F0.wireOp",EDGE,"E152"),sQuery(id+"F0.wireOp",EDGE,"E153"),sQuery(id+"F0.wireOp",EDGE,"E154"),sQuery(id+"F0.wireOp",EDGE,"E155"),sQuery(id+"F0.wireOp",EDGE,"E156"),sQuery(id+"F0.wireOp",EDGE,"E157"),sQuery(id+"F0.wireOp",EDGE,"E158"),sQuery(id+"F0.wireOp",EDGE,"E159"),sQuery(id+"F0.wireOp",EDGE,"E160"),sQuery(id+"F0.wireOp",EDGE,"E161"),sQuery(id+"F0.wireOp",EDGE,"E162"),sQuery(id+"F0.wireOp",EDGE,"E163"),sQuery(id+"F0.wireOp",EDGE,"E164"),sQuery(id+"F0.wireOp",EDGE,"E165"),sQuery(id+"F0.wireOp",EDGE,"E166"),sQuery(id+"F0.wireOp",EDGE,"E167"),sQuery(id+"F0.wireOp",EDGE,"E168"),sQuery(id+"F0.wireOp",EDGE,"E169"),sQuery(id+"F0.wireOp",EDGE,"E170"),sQuery(id+"F0.wireOp",EDGE,"E171"),sQuery(id+"F0.wireOp",EDGE,"E172"),sQuery(id+"F0.wireOp",EDGE,"E173"),sQuery(id+"F0.wireOp",EDGE,"E174")])],"isStart":true});
            extrude(context, id + "F3", {"entities" : qUnion([Q0]), "operationType" : NewBodyOperationType.ADD, "depth" : 10 * mm, "offsetDistance" : 25 * mm});
        }
        {
            var Q0;
            Q0=makeQuery(id+"F3.opExtrude","CAP_FACE",FACE,{"disambiguationData":[OSD([sQuery(id+"F0.wireOp",EDGE,"E0"),sQuery(id+"F0.wireOp",EDGE,"E1"),sQuery(id+"F0.wireOp",EDGE,"E2"),sQuery(id+"F0.wireOp",EDGE,"E3"),sQuery(id+"F0.wireOp",EDGE,"E4"),sQuery(id+"F0.wireOp",EDGE,"E5"),sQuery(id+"F0.wireOp",EDGE,"E6"),sQuery(id+"F0.wireOp",EDGE,"E7"),sQuery(id+"F0.wireOp",EDGE,"E8"),sQuery(id+"F0.wireOp",EDGE,"E9"),sQuery(id+"F0.wireOp",EDGE,"E10"),sQuery(id+"F0.wireOp",EDGE,"E11"),sQuery(id+"F0.wireOp",EDGE,"E12"),sQuery(id+"F0.wireOp",EDGE,"E13"),sQuery(id+"F0.wireOp",EDGE,"E14"),sQuery(id+"F0.wireOp",EDGE,"E15"),sQuery(id+"F0.wireOp",EDGE,"E16"),sQuery(id+"F0.wireOp",EDGE,"E17"),sQuery(id+"F0.wireOp",EDGE,"E18"),sQuery(id+"F0.wireOp",EDGE,"E19"),sQuery(id+"F0.wireOp",EDGE,"E20"),sQuery(id+"F0.wireOp",EDGE,"E21"),sQuery(id+"F0.wireOp",EDGE,"E22"),sQuery(id+"F0.wireOp",EDGE,"E23"),sQuery(id+"F0.wireOp",EDGE,"E24"),sQuery(id+"F0.wireOp",EDGE,"E25"),sQuery(id+"F0.wireOp",EDGE,"E26"),sQuery(id+"F0.wireOp",EDGE,"E27"),sQuery(id+"F0.wireOp",EDGE,"E28"),sQuery(id+"F0.wireOp",EDGE,"E29"),sQuery(id+"F0.wireOp",EDGE,"E30"),sQuery(id+"F0.wireOp",EDGE,"E31"),sQuery(id+"F0.wireOp",EDGE,"E32"),sQuery(id+"F0.wireOp",EDGE,"E33"),sQuery(id+"F0.wireOp",EDGE,"E34"),sQuery(id+"F0.wireOp",EDGE,"E35"),sQuery(id+"F0.wireOp",EDGE,"E36"),sQuery(id+"F0.wireOp",EDGE,"E37"),sQuery(id+"F0.wireOp",EDGE,"E38"),sQuery(id+"F0.wireOp",EDGE,"E39"),sQuery(id+"F0.wireOp",EDGE,"E40"),sQuery(id+"F0.wireOp",EDGE,"E41"),sQuery(id+"F0.wireOp",EDGE,"E42"),sQuery(id+"F0.wireOp",EDGE,"E43"),sQuery(id+"F0.wireOp",EDGE,"E44"),sQuery(id+"F0.wireOp",EDGE,"E45"),sQuery(id+"F0.wireOp",EDGE,"E46"),sQuery(id+"F0.wireOp",EDGE,"E47"),sQuery(id+"F0.wireOp",EDGE,"E48"),sQuery(id+"F0.wireOp",EDGE,"E49"),sQuery(id+"F0.wireOp",EDGE,"E50"),sQuery(id+"F0.wireOp",EDGE,"E51"),sQuery(id+"F0.wireOp",EDGE,"E52"),sQuery(id+"F0.wireOp",EDGE,"E53"),sQuery(id+"F0.wireOp",EDGE,"E54"),sQuery(id+"F0.wireOp",EDGE,"E55"),sQuery(id+"F0.wireOp",EDGE,"E56"),sQuery(id+"F0.wireOp",EDGE,"E57"),sQuery(id+"F0.wireOp",EDGE,"E58"),sQuery(id+"F0.wireOp",EDGE,"E59"),sQuery(id+"F0.wireOp",EDGE,"E60"),sQuery(id+"F0.wireOp",EDGE,"E61"),sQuery(id+"F0.wireOp",EDGE,"E62"),sQuery(id+"F0.wireOp",EDGE,"E63"),sQuery(id+"F0.wireOp",EDGE,"E64"),sQuery(id+"F0.wireOp",EDGE,"E65"),sQuery(id+"F0.wireOp",EDGE,"E66"),sQuery(id+"F0.wireOp",EDGE,"E67"),sQuery(id+"F0.wireOp",EDGE,"E68"),sQuery(id+"F0.wireOp",EDGE,"E69"),sQuery(id+"F0.wireOp",EDGE,"E70"),sQuery(id+"F0.wireOp",EDGE,"E71"),sQuery(id+"F0.wireOp",EDGE,"E72"),sQuery(id+"F0.wireOp",EDGE,"E73"),sQuery(id+"F0.wireOp",EDGE,"E74"),sQuery(id+"F0.wireOp",EDGE,"E75"),sQuery(id+"F0.wireOp",EDGE,"E76"),sQuery(id+"F0.wireOp",EDGE,"E77"),sQuery(id+"F0.wireOp",EDGE,"E78"),sQuery(id+"F0.wireOp",EDGE,"E79"),sQuery(id+"F0.wireOp",EDGE,"E80"),sQuery(id+"F0.wireOp",EDGE,"E81"),sQuery(id+"F0.wireOp",EDGE,"E82"),sQuery(id+"F0.wireOp",EDGE,"E83"),sQuery(id+"F0.wireOp",EDGE,"E84"),sQuery(id+"F0.wireOp",EDGE,"E85"),sQuery(id+"F0.wireOp",EDGE,"E86"),sQuery(id+"F0.wireOp",EDGE,"E87"),sQuery(id+"F0.wireOp",EDGE,"E88"),sQuery(id+"F0.wireOp",EDGE,"E89"),sQuery(id+"F0.wireOp",EDGE,"E90"),sQuery(id+"F0.wireOp",EDGE,"E91"),sQuery(id+"F0.wireOp",EDGE,"E92"),sQuery(id+"F0.wireOp",EDGE,"E92"),sQuery(id+"F0.wireOp",EDGE,"E92"),sQuery(id+"F0.wireOp",EDGE,"E92"),sQuery(id+"F0.wireOp",EDGE,"E92"),sQuery(id+"F0.wireOp",EDGE,"E93"),sQuery(id+"F0.wireOp",EDGE,"E94"),sQuery(id+"F0.wireOp",EDGE,"E94"),sQuery(id+"F0.wireOp",EDGE,"E95"),sQuery(id+"F0.wireOp",EDGE,"E96"),sQuery(id+"F0.wireOp",EDGE,"E97"),sQuery(id+"F0.wireOp",EDGE,"E98"),sQuery(id+"F0.wireOp",EDGE,"E99"),sQuery(id+"F0.wireOp",EDGE,"E100"),sQuery(id+"F0.wireOp",EDGE,"E101"),sQuery(id+"F0.wireOp",EDGE,"E102"),sQuery(id+"F0.wireOp",EDGE,"E103"),sQuery(id+"F0.wireOp",EDGE,"E104"),sQuery(id+"F0.wireOp",EDGE,"E105"),sQuery(id+"F0.wireOp",EDGE,"E106"),sQuery(id+"F0.wireOp",EDGE,"E107"),sQuery(id+"F0.wireOp",EDGE,"E108"),sQuery(id+"F0.wireOp",EDGE,"E109"),sQuery(id+"F0.wireOp",EDGE,"E110"),sQuery(id+"F0.wireOp",EDGE,"E111"),sQuery(id+"F0.wireOp",EDGE,"E112"),sQuery(id+"F0.wireOp",EDGE,"E113"),sQuery(id+"F0.wireOp",EDGE,"E114"),sQuery(id+"F0.wireOp",EDGE,"E115"),sQuery(id+"F0.wireOp",EDGE,"E116"),sQuery(id+"F0.wireOp",EDGE,"E116"),sQuery(id+"F0.wireOp",EDGE,"E117"),sQuery(id+"F0.wireOp",EDGE,"E118"),sQuery(id+"F0.wireOp",EDGE,"E119"),sQuery(id+"F0.wireOp",EDGE,"E120"),sQuery(id+"F0.wireOp",EDGE,"E121"),sQuery(id+"F0.wireOp",EDGE,"E122"),sQuery(id+"F0.wireOp",EDGE,"E123"),sQuery(id+"F0.wireOp",EDGE,"E124"),sQuery(id+"F0.wireOp",EDGE,"E125"),sQuery(id+"F0.wireOp",EDGE,"E126"),sQuery(id+"F0.wireOp",EDGE,"E127"),sQuery(id+"F0.wireOp",EDGE,"E128"),sQuery(id+"F0.wireOp",EDGE,"E129"),sQuery(id+"F0.wireOp",EDGE,"E130"),sQuery(id+"F0.wireOp",EDGE,"E131"),sQuery(id+"F0.wireOp",EDGE,"E132"),sQuery(id+"F0.wireOp",EDGE,"E133"),sQuery(id+"F0.wireOp",EDGE,"E134"),sQuery(id+"F0.wireOp",EDGE,"E135"),sQuery(id+"F0.wireOp",EDGE,"E136"),sQuery(id+"F0.wireOp",EDGE,"E137"),sQuery(id+"F0.wireOp",EDGE,"E138"),sQuery(id+"F0.wireOp",EDGE,"E139"),sQuery(id+"F0.wireOp",EDGE,"E139"),sQuery(id+"F0.wireOp",EDGE,"E140"),sQuery(id+"F0.wireOp",EDGE,"E141"),sQuery(id+"F0.wireOp",EDGE,"E141"),sQuery(id+"F0.wireOp",EDGE,"E142"),sQuery(id+"F0.wireOp",EDGE,"E143"),sQuery(id+"F0.wireOp",EDGE,"E143"),sQuery(id+"F0.wireOp",EDGE,"E143"),sQuery(id+"F0.wireOp",EDGE,"E144"),sQuery(id+"F0.wireOp",EDGE,"E145"),sQuery(id+"F0.wireOp",EDGE,"E146"),sQuery(id+"F0.wireOp",EDGE,"E147"),sQuery(id+"F0.wireOp",EDGE,"E148"),sQuery(id+"F0.wireOp",EDGE,"E149"),sQuery(id+"F0.wireOp",EDGE,"E150"),sQuery(id+"F0.wireOp",EDGE,"E151"),sQuery(id+"F0.wireOp",EDGE,"E152"),sQuery(id+"F0.wireOp",EDGE,"E153"),sQuery(id+"F0.wireOp",EDGE,"E154"),sQuery(id+"F0.wireOp",EDGE,"E155"),sQuery(id+"F0.wireOp",EDGE,"E156"),sQuery(id+"F0.wireOp",EDGE,"E157"),sQuery(id+"F0.wireOp",EDGE,"E158"),sQuery(id+"F0.wireOp",EDGE,"E159"),sQuery(id+"F0.wireOp",EDGE,"E160"),sQuery(id+"F0.wireOp",EDGE,"E161"),sQuery(id+"F0.wireOp",EDGE,"E162"),sQuery(id+"F0.wireOp",EDGE,"E163"),sQuery(id+"F0.wireOp",EDGE,"E164"),sQuery(id+"F0.wireOp",EDGE,"E165"),sQuery(id+"F0.wireOp",EDGE,"E166"),sQuery(id+"F0.wireOp",EDGE,"E167"),sQuery(id+"F0.wireOp",EDGE,"E168"),sQuery(id+"F0.wireOp",EDGE,"E169"),sQuery(id+"F0.wireOp",EDGE,"E170"),sQuery(id+"F0.wireOp",EDGE,"E171"),sQuery(id+"F0.wireOp",EDGE,"E172"),sQuery(id+"F0.wireOp",EDGE,"E173"),sQuery(id+"F0.wireOp",EDGE,"E174")])],"isStart":false});
            var Q1;
            Q1=makeQuery(id+"F1.opExtrude","SWEPT_BODY",BODY,{"disambiguationData":[OSD([sQuery(id+"F0.wireOp",EDGE,"E0"),sQuery(id+"F0.wireOp",EDGE,"E1"),sQuery(id+"F0.wireOp",EDGE,"E2"),sQuery(id+"F0.wireOp",EDGE,"E3"),sQuery(id+"F0.wireOp",EDGE,"E4"),sQuery(id+"F0.wireOp",EDGE,"E5"),sQuery(id+"F0.wireOp",EDGE,"E6"),sQuery(id+"F0.wireOp",EDGE,"E7"),sQuery(id+"F0.wireOp",EDGE,"E8"),sQuery(id+"F0.wireOp",EDGE,"E9"),sQuery(id+"F0.wireOp",EDGE,"E10"),sQuery(id+"F0.wireOp",EDGE,"E11"),sQuery(id+"F0.wireOp",EDGE,"E12"),sQuery(id+"F0.wireOp",EDGE,"E13"),sQuery(id+"F0.wireOp",EDGE,"E14"),sQuery(id+"F0.wireOp",EDGE,"E15"),sQuery(id+"F0.wireOp",EDGE,"E16"),sQuery(id+"F0.wireOp",EDGE,"E17"),sQuery(id+"F0.wireOp",EDGE,"E18"),sQuery(id+"F0.wireOp",EDGE,"E19"),sQuery(id+"F0.wireOp",EDGE,"E20"),sQuery(id+"F0.wireOp",EDGE,"E21"),sQuery(id+"F0.wireOp",EDGE,"E22"),sQuery(id+"F0.wireOp",EDGE,"E23"),sQuery(id+"F0.wireOp",EDGE,"E24"),sQuery(id+"F0.wireOp",EDGE,"E25"),sQuery(id+"F0.wireOp",EDGE,"E26"),sQuery(id+"F0.wireOp",EDGE,"E27"),sQuery(id+"F0.wireOp",EDGE,"E28"),sQuery(id+"F0.wireOp",EDGE,"E29"),sQuery(id+"F0.wireOp",EDGE,"E30"),sQuery(id+"F0.wireOp",EDGE,"E31"),sQuery(id+"F0.wireOp",EDGE,"E32"),sQuery(id+"F0.wireOp",EDGE,"E33"),sQuery(id+"F0.wireOp",EDGE,"E34"),sQuery(id+"F0.wireOp",EDGE,"E35"),sQuery(id+"F0.wireOp",EDGE,"E36"),sQuery(id+"F0.wireOp",EDGE,"E37"),sQuery(id+"F0.wireOp",EDGE,"E38"),sQuery(id+"F0.wireOp",EDGE,"E39"),sQuery(id+"F0.wireOp",EDGE,"E40"),sQuery(id+"F0.wireOp",EDGE,"E41"),sQuery(id+"F0.wireOp",EDGE,"E42"),sQuery(id+"F0.wireOp",EDGE,"E43"),sQuery(id+"F0.wireOp",EDGE,"E44"),sQuery(id+"F0.wireOp",EDGE,"E45"),sQuery(id+"F0.wireOp",EDGE,"E46"),sQuery(id+"F0.wireOp",EDGE,"E47"),sQuery(id+"F0.wireOp",EDGE,"E48"),sQuery(id+"F0.wireOp",EDGE,"E49"),sQuery(id+"F0.wireOp",EDGE,"E50"),sQuery(id+"F0.wireOp",EDGE,"E51"),sQuery(id+"F0.wireOp",EDGE,"E52"),sQuery(id+"F0.wireOp",EDGE,"E53"),sQuery(id+"F0.wireOp",EDGE,"E54"),sQuery(id+"F0.wireOp",EDGE,"E55"),sQuery(id+"F0.wireOp",EDGE,"E56"),sQuery(id+"F0.wireOp",EDGE,"E57"),sQuery(id+"F0.wireOp",EDGE,"E58"),sQuery(id+"F0.wireOp",EDGE,"E59"),sQuery(id+"F0.wireOp",EDGE,"E60"),sQuery(id+"F0.wireOp",EDGE,"E61"),sQuery(id+"F0.wireOp",EDGE,"E62"),sQuery(id+"F0.wireOp",EDGE,"E63"),sQuery(id+"F0.wireOp",EDGE,"E64"),sQuery(id+"F0.wireOp",EDGE,"E65"),sQuery(id+"F0.wireOp",EDGE,"E66"),sQuery(id+"F0.wireOp",EDGE,"E67"),sQuery(id+"F0.wireOp",EDGE,"E68"),sQuery(id+"F0.wireOp",EDGE,"E69"),sQuery(id+"F0.wireOp",EDGE,"E70"),sQuery(id+"F0.wireOp",EDGE,"E71"),sQuery(id+"F0.wireOp",EDGE,"E72"),sQuery(id+"F0.wireOp",EDGE,"E73"),sQuery(id+"F0.wireOp",EDGE,"E74"),sQuery(id+"F0.wireOp",EDGE,"E75"),sQuery(id+"F0.wireOp",EDGE,"E76"),sQuery(id+"F0.wireOp",EDGE,"E77"),sQuery(id+"F0.wireOp",EDGE,"E78"),sQuery(id+"F0.wireOp",EDGE,"E79"),sQuery(id+"F0.wireOp",EDGE,"E80"),sQuery(id+"F0.wireOp",EDGE,"E81"),sQuery(id+"F0.wireOp",EDGE,"E82"),sQuery(id+"F0.wireOp",EDGE,"E83"),sQuery(id+"F0.wireOp",EDGE,"E84"),sQuery(id+"F0.wireOp",EDGE,"E85"),sQuery(id+"F0.wireOp",EDGE,"E86"),sQuery(id+"F0.wireOp",EDGE,"E87"),sQuery(id+"F0.wireOp",EDGE,"E88"),sQuery(id+"F0.wireOp",EDGE,"E89"),sQuery(id+"F0.wireOp",EDGE,"E90"),sQuery(id+"F0.wireOp",EDGE,"E91"),sQuery(id+"F0.wireOp",EDGE,"E92"),sQuery(id+"F0.wireOp",EDGE,"E92"),sQuery(id+"F0.wireOp",EDGE,"E92"),sQuery(id+"F0.wireOp",EDGE,"E92"),sQuery(id+"F0.wireOp",EDGE,"E92"),sQuery(id+"F0.wireOp",EDGE,"E93"),sQuery(id+"F0.wireOp",EDGE,"E94"),sQuery(id+"F0.wireOp",EDGE,"E94"),sQuery(id+"F0.wireOp",EDGE,"E95"),sQuery(id+"F0.wireOp",EDGE,"E96"),sQuery(id+"F0.wireOp",EDGE,"E97"),sQuery(id+"F0.wireOp",EDGE,"E98"),sQuery(id+"F0.wireOp",EDGE,"E99"),sQuery(id+"F0.wireOp",EDGE,"E100"),sQuery(id+"F0.wireOp",EDGE,"E101"),sQuery(id+"F0.wireOp",EDGE,"E102"),sQuery(id+"F0.wireOp",EDGE,"E103"),sQuery(id+"F0.wireOp",EDGE,"E104"),sQuery(id+"F0.wireOp",EDGE,"E105"),sQuery(id+"F0.wireOp",EDGE,"E106"),sQuery(id+"F0.wireOp",EDGE,"E107"),sQuery(id+"F0.wireOp",EDGE,"E108"),sQuery(id+"F0.wireOp",EDGE,"E109"),sQuery(id+"F0.wireOp",EDGE,"E110"),sQuery(id+"F0.wireOp",EDGE,"E111"),sQuery(id+"F0.wireOp",EDGE,"E112"),sQuery(id+"F0.wireOp",EDGE,"E113"),sQuery(id+"F0.wireOp",EDGE,"E114"),sQuery(id+"F0.wireOp",EDGE,"E115"),sQuery(id+"F0.wireOp",EDGE,"E116"),sQuery(id+"F0.wireOp",EDGE,"E116"),sQuery(id+"F0.wireOp",EDGE,"E117"),sQuery(id+"F0.wireOp",EDGE,"E118"),sQuery(id+"F0.wireOp",EDGE,"E119"),sQuery(id+"F0.wireOp",EDGE,"E120"),sQuery(id+"F0.wireOp",EDGE,"E121"),sQuery(id+"F0.wireOp",EDGE,"E122"),sQuery(id+"F0.wireOp",EDGE,"E123"),sQuery(id+"F0.wireOp",EDGE,"E124"),sQuery(id+"F0.wireOp",EDGE,"E125"),sQuery(id+"F0.wireOp",EDGE,"E126"),sQuery(id+"F0.wireOp",EDGE,"E127"),sQuery(id+"F0.wireOp",EDGE,"E128"),sQuery(id+"F0.wireOp",EDGE,"E129"),sQuery(id+"F0.wireOp",EDGE,"E130"),sQuery(id+"F0.wireOp",EDGE,"E131"),sQuery(id+"F0.wireOp",EDGE,"E132"),sQuery(id+"F0.wireOp",EDGE,"E133"),sQuery(id+"F0.wireOp",EDGE,"E134"),sQuery(id+"F0.wireOp",EDGE,"E135"),sQuery(id+"F0.wireOp",EDGE,"E136"),sQuery(id+"F0.wireOp",EDGE,"E137"),sQuery(id+"F0.wireOp",EDGE,"E138"),sQuery(id+"F0.wireOp",EDGE,"E139"),sQuery(id+"F0.wireOp",EDGE,"E139"),sQuery(id+"F0.wireOp",EDGE,"E140"),sQuery(id+"F0.wireOp",EDGE,"E141"),sQuery(id+"F0.wireOp",EDGE,"E141"),sQuery(id+"F0.wireOp",EDGE,"E142"),sQuery(id+"F0.wireOp",EDGE,"E143"),sQuery(id+"F0.wireOp",EDGE,"E143"),sQuery(id+"F0.wireOp",EDGE,"E143"),sQuery(id+"F0.wireOp",EDGE,"E144"),sQuery(id+"F0.wireOp",EDGE,"E145"),sQuery(id+"F0.wireOp",EDGE,"E146"),sQuery(id+"F0.wireOp",EDGE,"E147"),sQuery(id+"F0.wireOp",EDGE,"E148"),sQuery(id+"F0.wireOp",EDGE,"E149"),sQuery(id+"F0.wireOp",EDGE,"E150"),sQuery(id+"F0.wireOp",EDGE,"E151"),sQuery(id+"F0.wireOp",EDGE,"E152"),sQuery(id+"F0.wireOp",EDGE,"E153"),sQuery(id+"F0.wireOp",EDGE,"E154"),sQuery(id+"F0.wireOp",EDGE,"E155"),sQuery(id+"F0.wireOp",EDGE,"E156"),sQuery(id+"F0.wireOp",EDGE,"E157"),sQuery(id+"F0.wireOp",EDGE,"E158"),sQuery(id+"F0.wireOp",EDGE,"E159"),sQuery(id+"F0.wireOp",EDGE,"E160"),sQuery(id+"F0.wireOp",EDGE,"E161"),sQuery(id+"F0.wireOp",EDGE,"E162"),sQuery(id+"F0.wireOp",EDGE,"E163"),sQuery(id+"F0.wireOp",EDGE,"E164"),sQuery(id+"F0.wireOp",EDGE,"E165"),sQuery(id+"F0.wireOp",EDGE,"E166"),sQuery(id+"F0.wireOp",EDGE,"E167"),sQuery(id+"F0.wireOp",EDGE,"E168"),sQuery(id+"F0.wireOp",EDGE,"E169"),sQuery(id+"F0.wireOp",EDGE,"E170"),sQuery(id+"F0.wireOp",EDGE,"E171"),sQuery(id+"F0.wireOp",EDGE,"E172"),sQuery(id+"F0.wireOp",EDGE,"E173"),sQuery(id+"F0.wireOp",EDGE,"E174")])]});
            shell(context, id + "F4", {"entities" : qUnion([Q0]), "parts" : qUnion([Q1]), "thickness" : 2 * mm});
        }
    });
